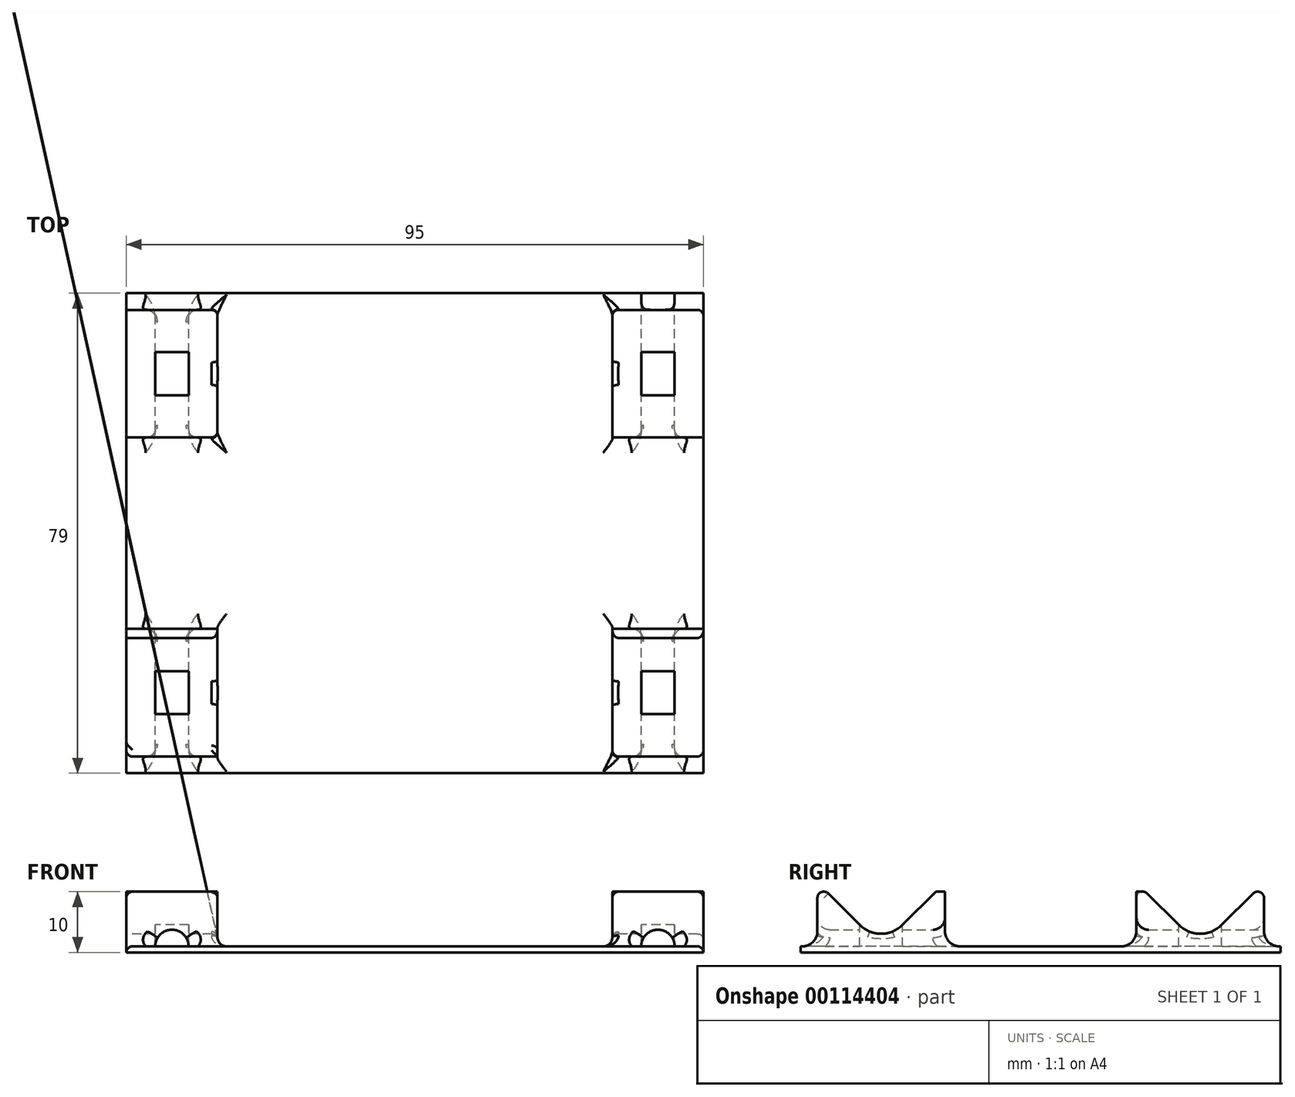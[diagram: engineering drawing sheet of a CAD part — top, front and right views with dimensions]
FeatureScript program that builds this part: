
annotation { "Feature Type Name" : "Feature", "Feature Type Description" : "" }
export const myFeature = defineFeature(function(context is Context, id is Id, definition is map)
    precondition{}
    {
        {
            var Q0;
            Q0=qCreatedBy(makeId("Top.planeOp"),FACE);
            var sketch = newSketch(context, id + "F0", { "sketchPlane" : qUnion([Q0])});
            skLineSegment(sketch, "E0.bottom", {"start": v(0, 0) * mm, "end": v(95, 0) * mm});
            skLineSegment(sketch, "E0.top", {"start": v(0, 79) * mm, "end": v(95, 79) * mm});
            skLineSegment(sketch, "E0.left", {"start": v(0, 0) * mm, "end": v(0, 79) * mm});
            skLineSegment(sketch, "E0.right", {"start": v(95, 0) * mm, "end": v(95, 79) * mm});
            skSolve(sketch);
        }
        {
            var Q0;
            Q0=makeQuery(id+"F0.imprint","IMPRINT",FACE,{"disambiguationData":[TD([[makeQuery(id+"F0.imprint","IMPRINT",EDGE,{"derivedFrom":sQuery(id+"F0.wireOp",EDGE,"E0.bottom")}),1.0]])]});
            extrude(context, id + "F1", {"entities" : qUnion([Q0]), "depth" : 10 * mm});
        }
        {
            var Q0;
            Q0=qCreatedBy(makeId("Right.planeOp"),FACE);
            var sketch = newSketch(context, id + "F2", { "sketchPlane" : qUnion([Q0])});
            skCircle(sketch, "E1", {"center": v(65.75, 10.55) * mm, "radius": 6.75 * mm, "construction": true});
            skLineSegment(sketch, "E2", {"start": v(79, 1) * mm, "end": v(0, 1) * mm, "construction": true});
            skLineSegment(sketch, "E3.0", {"start": v(79, 10) * mm, "end": v(79, 0) * mm, "construction": true});
            skLineSegment(sketch, "E4.0", {"start": v(0, 10) * mm, "end": v(0, 0) * mm, "construction": true});
            skLineSegment(sketch, "E5", {"start": v(79, 0) * mm, "end": v(0, 0) * mm, "construction": true});
            skLineSegment(sketch, "E6", {"start": v(39.5, 0) * mm, "end": v(39.5, 0) * mm});
            skPoint(sketch, "E6.endSnap0", {"position": v(39.5, 0) * mm});
            skLineSegment(sketch, "E7.0", {"start": v(0, 10) * mm, "end": v(79, 10) * mm});
            skLineSegment(sketch, "E8", {"start": v(65.75, 1) * mm, "end": v(74.75, 10) * mm});
            skLineSegment(sketch, "E9", {"start": v(65.75, 1) * mm, "end": v(56.75, 10) * mm});
            skLineSegment(sketch, "E10", {"start": v(39.5, 0) * mm, "end": v(39.5, 10) * mm, "construction": true});
            skLineSegment(sketch, "E11", {"start": v(74.75, 10) * mm, "end": v(76.25, 10) * mm, "construction": true});
            skLineSegment(sketch, "E12", {"start": v(76.25, 10) * mm, "end": v(76.25, 1) * mm});
            skLineSegment(sketch, "E13", {"start": v(76.25, 1) * mm, "end": v(79, 1) * mm});
            skLineSegment(sketch, "E14", {"start": v(79, 10) * mm, "end": v(76.25, 10) * mm});
            skLineSegment(sketch, "E15", {"start": v(79, 10) * mm, "end": v(79, 1) * mm});
            skLineSegment(sketch, "E16", {"start": v(56.75, 10) * mm, "end": v(55.25, 10) * mm, "construction": true});
            skLineSegment(sketch, "E17", {"start": v(55.25, 10) * mm, "end": v(55.25, 1) * mm});
            skLineSegment(sketch, "E18", {"start": v(55.25, 1) * mm, "end": v(39.5, 1) * mm});
            skLineSegment(sketch, "E19.MirrorCS", {"start": v(0, 10) * mm, "end": v(2.75, 10) * mm});
            skLineSegment(sketch, "E20.MirrorCS", {"start": v(2.75, 10) * mm, "end": v(2.75, 1) * mm});
            skLineSegment(sketch, "E21.MirrorCS", {"start": v(13.25, 1) * mm, "end": v(4.25, 10) * mm});
            skLineSegment(sketch, "E22.MirrorCS", {"start": v(13.25, 1) * mm, "end": v(22.25, 10) * mm});
            skLineSegment(sketch, "E23.MirrorCS", {"start": v(4.25, 10) * mm, "end": v(2.75, 10) * mm});
            skLineSegment(sketch, "E24.MirrorCS", {"start": v(22.25, 10) * mm, "end": v(23.75, 10) * mm});
            skLineSegment(sketch, "E25.MirrorCS", {"start": v(23.75, 10) * mm, "end": v(23.75, 1) * mm});
            skLineSegment(sketch, "E26.MirrorCS", {"start": v(2.75, 1) * mm, "end": v(0, 1) * mm});
            skLineSegment(sketch, "E27.MirrorCS", {"start": v(0, 10) * mm, "end": v(0, 1) * mm});
            skLineSegment(sketch, "E28.MirrorCS", {"start": v(23.75, 1) * mm, "end": v(39.5, 1) * mm});
            skLineSegment(sketch, "E29", {"start": v(39.5, 10) * mm, "end": v(39.5, 15.62) * mm, "construction": true});
            skSolve(sketch);
        }
        {
            var Q0;
            Q0 = qSketchRegion(id + "F2", true);
            extrude(context, id + "F3", {"entities" : qUnion([Q0]), "operationType" : NewBodyOperationType.REMOVE, "endBound" : BoundingType.THROUGH_ALL, "depth" : 25 * mm});
        }
        {
            var Q0;
            Q0=makeQuery(id+"F3.boolean.opBoolean","COPY",EDGE,{"derivedFrom":makeQuery(id+"F3.opExtrude","SWEPT_EDGE",EDGE,{"disambiguationData":[OSD([sQuery(id+"F2.wireOp",EDGE,"E8"),sQuery(id+"F2.wireOp",EDGE,"E9")])]})});
            var Q1;
            Q1=makeQuery(id+"F3.boolean.opBoolean","COPY",EDGE,{"derivedFrom":makeQuery(id+"F3.opExtrude","SWEPT_EDGE",EDGE,{"disambiguationData":[OSD([sQuery(id+"F2.wireOp",EDGE,"E21.MirrorCS"),sQuery(id+"F2.wireOp",EDGE,"E22.MirrorCS")])]})});
            fillet(context, id + "F4", {"entities" : qUnion([Q0, Q1]), "radius" : 5 * mm, "tangentPropagation" : true, "allowEdgeOverflow" : false});
        }
        {
            var Q0;
            Q0=qCreatedBy(makeId("Front.planeOp"),FACE);
            var sketch = newSketch(context, id + "F5", { "sketchPlane" : qUnion([Q0])});
            skLineSegment(sketch, "E30.top", {"start": v(15, 10) * mm, "end": v(80, 10) * mm});
            skLineSegment(sketch, "E30.left", {"start": v(15, 1) * mm, "end": v(15, 10) * mm});
            skLineSegment(sketch, "E30.right", {"start": v(80, 1) * mm, "end": v(80, 10) * mm});
            skLineSegment(sketch, "E31.0", {"start": v(95, 1) * mm, "end": v(0, 1) * mm});
            skSolve(sketch);
        }
        {
            var Q0;
            Q0=makeQuery(id+"F5.imprint","IMPRINT",FACE,{"disambiguationData":[TD([[makeQuery(id+"F5.imprint","IMPRINT",EDGE,{"derivedFrom":sQuery(id+"F5.wireOp",EDGE,"E30.top")}),-1.0]])]});
            extrude(context, id + "F6", {"entities" : qUnion([Q0]), "operationType" : NewBodyOperationType.REMOVE, "endBound" : BoundingType.THROUGH_ALL, "oppositeDirection" : true, "depth" : 25 * mm});
        }
        {
            var Q0;
            {var subQ0=sQuery(id+"F0.wireOp",EDGE,"E0.left");Q0=makeQuery(id+"F6.boolean.opBoolean","SPLIT",FACE,{"disambiguationData":[TD([makeQuery(id+"F1.opExtrude","SWEPT_FACE",FACE,{"disambiguationData":[OSD([subQ0])]})])],"derivedFrom":makeQuery(id+"F3.boolean.opBoolean","COPY",FACE,{"derivedFrom":makeQuery(id+"F3.opExtrude","SWEPT_FACE",FACE,{"disambiguationData":[OSD([sQuery(id+"F2.wireOp",EDGE,"E12")])]})})});}
            var sketch = newSketch(context, id + "F7", { "sketchPlane" : qUnion([Q0])});
            skLineSegment(sketch, "E32.0", {"start": v(-15, 10) * mm, "end": v(-15, 1) * mm, "construction": true});
            skLineSegment(sketch, "E33.0", {"start": v(0, 10) * mm, "end": v(0, 1) * mm, "construction": true});
            skLineSegment(sketch, "E34.0", {"start": v(-15, 10) * mm, "end": v(0, 10) * mm, "construction": true});
            skLineSegment(sketch, "E35.0", {"start": v(-15, 1) * mm, "end": v(0, 1) * mm, "construction": true});
            skLineSegment(sketch, "E36.0", {"start": v(-95, 10) * mm, "end": v(-95, 1) * mm, "construction": true});
            skLineSegment(sketch, "E37.0", {"start": v(-80, 10) * mm, "end": v(-80, 1) * mm, "construction": true});
            skLineSegment(sketch, "E38.0", {"start": v(-95, 1) * mm, "end": v(-80, 1) * mm, "construction": true});
            skLineSegment(sketch, "E39.0", {"start": v(-95, 10) * mm, "end": v(-80, 10) * mm, "construction": true});
            skArc(sketch, "E40", {"start": v(-84.75, 1) * mm, "mid": v(-87.5, 3.75) * mm, "end": v(-90.25, 1) * mm});
            skLineSegment(sketch, "E41", {"start": v(-90.25, 1) * mm, "end": v(-84.75, 1) * mm});
            skArc(sketch, "E42", {"start": v(-4.75, 1) * mm, "mid": v(-7.5, 3.75) * mm, "end": v(-10.25, 1) * mm});
            skLineSegment(sketch, "E43", {"start": v(-10.25, 1) * mm, "end": v(-4.75, 1) * mm});
            skSolve(sketch);
        }
        {
            var Q0;
            Q0 = qSketchRegion(id + "F7", true);
            extrude(context, id + "F8", {"entities" : qUnion([Q0]), "operationType" : NewBodyOperationType.REMOVE, "endBound" : BoundingType.THROUGH_ALL, "oppositeDirection" : true, "depth" : 25 * mm});
        }
        {
            var Q0;
            {var subQ0=sQuery(id+"F0.wireOp",EDGE,"E0.right");var subQ1=makeQuery(id+"F1.opExtrude","SWEPT_FACE",FACE,{"disambiguationData":[OSD([subQ0])]});var subQ2=makeQuery(id+"F3.opExtrude","SWEPT_FACE",FACE,{"disambiguationData":[OSD([sQuery(id+"F2.wireOp",EDGE,"E20.MirrorCS")])]});var subQ4=sQuery(id+"F0.wireOp",EDGE,"E0.left");Q0=makeQuery(id+"F6.boolean.opBoolean","SPLIT",FACE,{"disambiguationData":[TD([subQ1])],"derivedFrom":makeQuery(id+"F3.boolean.opBoolean","SPLIT",FACE,{"disambiguationData":[TD([subQ2])],"derivedFrom":makeQuery(id+"F1.opExtrude","CAP_FACE",FACE,{"disambiguationData":[OSD([sQuery(id+"F0.wireOp",EDGE,"E0.bottom"),sQuery(id+"F0.wireOp",EDGE,"E0.top"),subQ4,subQ0])],"isStart":false})})});}
            var sketch = newSketch(context, id + "F9", { "sketchPlane" : qUnion([Q0])});
            skLineSegment(sketch, "E44.0", {"start": v(95, 62.21) * mm, "end": v(80, 62.21) * mm});
            skLineSegment(sketch, "E45.0", {"start": v(80, 69.29) * mm, "end": v(95, 69.29) * mm});
            skLineSegment(sketch, "E46", {"start": v(87.5, 62.21) * mm, "end": v(87.5, 69.29) * mm, "construction": true});
            skLineSegment(sketch, "E47.bottom", {"start": v(90.25, 62.21) * mm, "end": v(84.75, 62.21) * mm});
            skLineSegment(sketch, "E47.top", {"start": v(90.25, 69.29) * mm, "end": v(84.75, 69.29) * mm});
            skLineSegment(sketch, "E47.left", {"start": v(90.25, 62.21) * mm, "end": v(90.25, 69.29) * mm});
            skLineSegment(sketch, "E47.right", {"start": v(84.75, 62.21) * mm, "end": v(84.75, 69.29) * mm});
            skLineSegment(sketch, "E48.0", {"start": v(95, 9.71) * mm, "end": v(80, 9.71) * mm, "construction": true});
            skLineSegment(sketch, "E48.1", {"start": v(80, 16.79) * mm, "end": v(95, 16.79) * mm, "construction": true});
            skLineSegment(sketch, "E49", {"start": v(87.5, 9.71) * mm, "end": v(87.5, 16.79) * mm, "construction": true});
            skLineSegment(sketch, "E50.bottom", {"start": v(90.25, 9.71) * mm, "end": v(84.75, 9.71) * mm});
            skLineSegment(sketch, "E50.top", {"start": v(90.25, 16.79) * mm, "end": v(84.75, 16.79) * mm});
            skLineSegment(sketch, "E50.left", {"start": v(90.25, 9.71) * mm, "end": v(90.25, 16.79) * mm});
            skLineSegment(sketch, "E50.right", {"start": v(84.75, 9.71) * mm, "end": v(84.75, 16.79) * mm});
            skLineSegment(sketch, "E51.0", {"start": v(15, 9.71) * mm, "end": v(0, 9.71) * mm});
            skLineSegment(sketch, "E51.1", {"start": v(0, 16.79) * mm, "end": v(15, 16.79) * mm});
            skLineSegment(sketch, "E51.2", {"start": v(15, 62.21) * mm, "end": v(0, 62.21) * mm});
            skLineSegment(sketch, "E51.3", {"start": v(0, 69.29) * mm, "end": v(15, 69.29) * mm});
            skLineSegment(sketch, "E52", {"start": v(7.5, 9.71) * mm, "end": v(7.5, 69.29) * mm, "construction": true});
            skLineSegment(sketch, "E53.bottom", {"start": v(4.75, 69.29) * mm, "end": v(10.25, 69.29) * mm});
            skLineSegment(sketch, "E53.top", {"start": v(4.75, 62.21) * mm, "end": v(10.25, 62.21) * mm});
            skLineSegment(sketch, "E53.left", {"start": v(4.75, 69.29) * mm, "end": v(4.75, 62.21) * mm});
            skLineSegment(sketch, "E53.right", {"start": v(10.25, 69.29) * mm, "end": v(10.25, 62.21) * mm});
            skLineSegment(sketch, "E54.bottom", {"start": v(4.75, 16.79) * mm, "end": v(10.25, 16.79) * mm});
            skLineSegment(sketch, "E54.top", {"start": v(4.75, 9.71) * mm, "end": v(10.25, 9.71) * mm});
            skLineSegment(sketch, "E54.left", {"start": v(4.75, 16.79) * mm, "end": v(4.75, 9.71) * mm});
            skLineSegment(sketch, "E54.right", {"start": v(10.25, 16.79) * mm, "end": v(10.25, 9.71) * mm});
            skSolve(sketch);
        }
        {
            var Q0;
            Q0 = qSketchRegion(id + "F9", true);
            var Q1;
            Q1=makeQuery(id+"F8.boolean.opBoolean","MERGE",FACE,{"derivedFrom":[makeQuery(id+"F6.boolean.opBoolean","MERGE",FACE,{"derivedFrom":[makeQuery(id+"F3.boolean.opBoolean","COPY",FACE,{"derivedFrom":makeQuery(id+"F3.opExtrude","SWEPT_FACE",FACE,{"disambiguationData":[OSD([sQuery(id+"F2.wireOp",EDGE,"E13")])]})}),makeQuery(id+"F3.boolean.opBoolean","COPY",FACE,{"derivedFrom":makeQuery(id+"F3.opExtrude","SWEPT_FACE",FACE,{"disambiguationData":[OSD([sQuery(id+"F2.wireOp",EDGE,"E18"),sQuery(id+"F2.wireOp",EDGE,"E28.MirrorCS")])]})}),makeQuery(id+"F3.boolean.opBoolean","COPY",FACE,{"derivedFrom":makeQuery(id+"F3.opExtrude","SWEPT_FACE",FACE,{"disambiguationData":[OSD([sQuery(id+"F2.wireOp",EDGE,"E26.MirrorCS")])]})}),makeQuery(id+"F6.opExtrude","SWEPT_FACE",FACE,{"disambiguationData":[OSD([sQuery(id+"F5.wireOp",EDGE,"E31.0")])]})]}),makeQuery(id+"F8.opExtrude","SWEPT_FACE",FACE,{"disambiguationData":[OSD([sQuery(id+"F7.wireOp",EDGE,"E41")])]}),makeQuery(id+"F8.opExtrude","SWEPT_FACE",FACE,{"disambiguationData":[OSD([sQuery(id+"F7.wireOp",EDGE,"E43")])]})]});
            extrude(context, id + "F10", {"entities" : qUnion([Q0]), "operationType" : NewBodyOperationType.REMOVE, "endBound" : BoundingType.UP_TO_SURFACE, "oppositeDirection" : true, "endBoundEntityFace" : qUnion([Q1]), "depth" : 25 * mm});
        }
        {
            var Q0;
            {var subQ0=sQuery(id+"F2.wireOp",EDGE,"E25.MirrorCS");var subQ2=makeQuery(id+"F1.opExtrude","SWEPT_FACE",FACE,{"disambiguationData":[OSD([sQuery(id+"F0.wireOp",EDGE,"E0.right")])]});var subQ3=sQuery(id+"F2.wireOp",EDGE,"E28.MirrorCS");Q0=makeQuery(id+"F8.boolean.opBoolean","SPLIT",EDGE,{"disambiguationData":[TD([subQ2])],"derivedFrom":makeQuery(id+"F6.boolean.opBoolean","SPLIT",EDGE,{"disambiguationData":[TD([subQ2])],"derivedFrom":makeQuery(id+"F3.boolean.opBoolean","COPY",EDGE,{"derivedFrom":makeQuery(id+"F3.opExtrude","SWEPT_EDGE",EDGE,{"disambiguationData":[OSD([subQ0,subQ3])]})})})});}
            var Q1;
            {var subQ1=sQuery(id+"F2.wireOp",EDGE,"E25.MirrorCS");var subQ3=sQuery(id+"F2.wireOp",EDGE,"E28.MirrorCS");var subQ9=sQuery(id+"F0.wireOp",EDGE,"E0.right");var subQ10=makeQuery(id+"F6.opExtrude","SWEPT_FACE",FACE,{"disambiguationData":[OSD([sQuery(id+"F5.wireOp",EDGE,"E30.right")])]});Q1=makeQuery(id+"F8.boolean.opBoolean","SPLIT",EDGE,{"disambiguationData":[TD([makeQuery(id+"F6.boolean.opBoolean","COPY",FACE,{"disambiguationData":[TD([makeQuery(id+"F3.boolean.opBoolean","COPY",FACE,{"derivedFrom":makeQuery(id+"F3.opExtrude","SWEPT_FACE",FACE,{"disambiguationData":[OSD([sQuery(id+"F2.wireOp",EDGE,"E20.MirrorCS")])]})})])],"derivedFrom":subQ10})])],"derivedFrom":makeQuery(id+"F6.boolean.opBoolean","SPLIT",EDGE,{"disambiguationData":[TD([makeQuery(id+"F1.opExtrude","SWEPT_FACE",FACE,{"disambiguationData":[OSD([subQ9])]})])],"derivedFrom":makeQuery(id+"F3.boolean.opBoolean","COPY",EDGE,{"derivedFrom":makeQuery(id+"F3.opExtrude","SWEPT_EDGE",EDGE,{"disambiguationData":[OSD([subQ1,subQ3])]})})})});}
            var Q2;
            {var subQ1=sQuery(id+"F2.wireOp",EDGE,"E13");var subQ3=sQuery(id+"F2.wireOp",EDGE,"E12");var subQ5=makeQuery(id+"F1.opExtrude","SWEPT_FACE",FACE,{"disambiguationData":[OSD([sQuery(id+"F0.wireOp",EDGE,"E0.right")])]});Q2=makeQuery(id+"F8.boolean.opBoolean","SPLIT",EDGE,{"disambiguationData":[TD([subQ5])],"derivedFrom":makeQuery(id+"F6.boolean.opBoolean","SPLIT",EDGE,{"disambiguationData":[TD([subQ5])],"derivedFrom":makeQuery(id+"F3.boolean.opBoolean","COPY",EDGE,{"derivedFrom":makeQuery(id+"F3.opExtrude","SWEPT_EDGE",EDGE,{"disambiguationData":[OSD([subQ3,subQ1])]})})})});}
            var Q3;
            {var subQ2=sQuery(id+"F2.wireOp",EDGE,"E13");var subQ4=sQuery(id+"F2.wireOp",EDGE,"E12");var subQ8=sQuery(id+"F0.wireOp",EDGE,"E0.right");var subQ9=sQuery(id+"F2.wireOp",EDGE,"E8");var subQ10=makeQuery(id+"F6.opExtrude","SWEPT_FACE",FACE,{"disambiguationData":[OSD([sQuery(id+"F5.wireOp",EDGE,"E30.right")])]});Q3=makeQuery(id+"F8.boolean.opBoolean","SPLIT",EDGE,{"disambiguationData":[TD([makeQuery(id+"F6.boolean.opBoolean","COPY",FACE,{"disambiguationData":[TD([makeQuery(id+"F3.boolean.opBoolean","COPY",FACE,{"derivedFrom":makeQuery(id+"F3.opExtrude","SWEPT_FACE",FACE,{"disambiguationData":[OSD([subQ9])]})})])],"derivedFrom":subQ10})])],"derivedFrom":makeQuery(id+"F6.boolean.opBoolean","SPLIT",EDGE,{"disambiguationData":[TD([makeQuery(id+"F1.opExtrude","SWEPT_FACE",FACE,{"disambiguationData":[OSD([subQ8])]})])],"derivedFrom":makeQuery(id+"F3.boolean.opBoolean","COPY",EDGE,{"derivedFrom":makeQuery(id+"F3.opExtrude","SWEPT_EDGE",EDGE,{"disambiguationData":[OSD([subQ4,subQ2])]})})})});}
            var Q4;
            {var subQ2=sQuery(id+"F2.wireOp",EDGE,"E12");var subQ5=sQuery(id+"F0.wireOp",EDGE,"E0.left");var subQ6=sQuery(id+"F2.wireOp",EDGE,"E8");var subQ7=sQuery(id+"F2.wireOp",EDGE,"E13");var subQ10=makeQuery(id+"F6.opExtrude","SWEPT_FACE",FACE,{"disambiguationData":[OSD([sQuery(id+"F5.wireOp",EDGE,"E30.left")])]});Q4=makeQuery(id+"F8.boolean.opBoolean","SPLIT",EDGE,{"disambiguationData":[TD([makeQuery(id+"F6.boolean.opBoolean","COPY",FACE,{"disambiguationData":[TD([makeQuery(id+"F3.boolean.opBoolean","COPY",FACE,{"derivedFrom":makeQuery(id+"F3.opExtrude","SWEPT_FACE",FACE,{"disambiguationData":[OSD([subQ6])]})})])],"derivedFrom":subQ10})])],"derivedFrom":makeQuery(id+"F6.boolean.opBoolean","SPLIT",EDGE,{"disambiguationData":[TD([makeQuery(id+"F1.opExtrude","SWEPT_FACE",FACE,{"disambiguationData":[OSD([subQ5])]})])],"derivedFrom":makeQuery(id+"F3.boolean.opBoolean","COPY",EDGE,{"derivedFrom":makeQuery(id+"F3.opExtrude","SWEPT_EDGE",EDGE,{"disambiguationData":[OSD([subQ2,subQ7])]})})})});}
            var Q5;
            {var subQ1=sQuery(id+"F2.wireOp",EDGE,"E13");var subQ3=sQuery(id+"F2.wireOp",EDGE,"E12");var subQ5=makeQuery(id+"F1.opExtrude","SWEPT_FACE",FACE,{"disambiguationData":[OSD([sQuery(id+"F0.wireOp",EDGE,"E0.left")])]});Q5=makeQuery(id+"F8.boolean.opBoolean","SPLIT",EDGE,{"disambiguationData":[TD([subQ5])],"derivedFrom":makeQuery(id+"F6.boolean.opBoolean","SPLIT",EDGE,{"disambiguationData":[TD([subQ5])],"derivedFrom":makeQuery(id+"F3.boolean.opBoolean","COPY",EDGE,{"derivedFrom":makeQuery(id+"F3.opExtrude","SWEPT_EDGE",EDGE,{"disambiguationData":[OSD([subQ3,subQ1])]})})})});}
            var Q6;
            {var subQ1=sQuery(id+"F2.wireOp",EDGE,"E25.MirrorCS");var subQ3=sQuery(id+"F2.wireOp",EDGE,"E28.MirrorCS");var subQ8=sQuery(id+"F0.wireOp",EDGE,"E0.left");var subQ10=makeQuery(id+"F6.opExtrude","SWEPT_FACE",FACE,{"disambiguationData":[OSD([sQuery(id+"F5.wireOp",EDGE,"E30.left")])]});Q6=makeQuery(id+"F8.boolean.opBoolean","SPLIT",EDGE,{"disambiguationData":[TD([makeQuery(id+"F6.boolean.opBoolean","COPY",FACE,{"disambiguationData":[TD([makeQuery(id+"F3.boolean.opBoolean","COPY",FACE,{"derivedFrom":makeQuery(id+"F3.opExtrude","SWEPT_FACE",FACE,{"disambiguationData":[OSD([sQuery(id+"F2.wireOp",EDGE,"E20.MirrorCS")])]})})])],"derivedFrom":subQ10})])],"derivedFrom":makeQuery(id+"F6.boolean.opBoolean","SPLIT",EDGE,{"disambiguationData":[TD([makeQuery(id+"F1.opExtrude","SWEPT_FACE",FACE,{"disambiguationData":[OSD([subQ8])]})])],"derivedFrom":makeQuery(id+"F3.boolean.opBoolean","COPY",EDGE,{"derivedFrom":makeQuery(id+"F3.opExtrude","SWEPT_EDGE",EDGE,{"disambiguationData":[OSD([subQ1,subQ3])]})})})});}
            var Q7;
            {var subQ0=sQuery(id+"F2.wireOp",EDGE,"E25.MirrorCS");var subQ2=sQuery(id+"F2.wireOp",EDGE,"E28.MirrorCS");var subQ5=makeQuery(id+"F1.opExtrude","SWEPT_FACE",FACE,{"disambiguationData":[OSD([sQuery(id+"F0.wireOp",EDGE,"E0.left")])]});Q7=makeQuery(id+"F8.boolean.opBoolean","SPLIT",EDGE,{"disambiguationData":[TD([subQ5])],"derivedFrom":makeQuery(id+"F6.boolean.opBoolean","SPLIT",EDGE,{"disambiguationData":[TD([subQ5])],"derivedFrom":makeQuery(id+"F3.boolean.opBoolean","COPY",EDGE,{"derivedFrom":makeQuery(id+"F3.opExtrude","SWEPT_EDGE",EDGE,{"disambiguationData":[OSD([subQ0,subQ2])]})})})});}
            var Q8;
            {var subQ0=sQuery(id+"F2.wireOp",EDGE,"E20.MirrorCS");var subQ4=makeQuery(id+"F1.opExtrude","SWEPT_FACE",FACE,{"disambiguationData":[OSD([sQuery(id+"F0.wireOp",EDGE,"E0.right")])]});var subQ5=sQuery(id+"F2.wireOp",EDGE,"E26.MirrorCS");Q8=makeQuery(id+"F8.boolean.opBoolean","SPLIT",EDGE,{"disambiguationData":[TD([subQ4])],"derivedFrom":makeQuery(id+"F6.boolean.opBoolean","SPLIT",EDGE,{"disambiguationData":[TD([subQ4])],"derivedFrom":makeQuery(id+"F3.boolean.opBoolean","COPY",EDGE,{"derivedFrom":makeQuery(id+"F3.opExtrude","SWEPT_EDGE",EDGE,{"disambiguationData":[OSD([subQ0,subQ5])]})})})});}
            var Q9;
            {var subQ0=sQuery(id+"F2.wireOp",EDGE,"E26.MirrorCS");var subQ2=sQuery(id+"F2.wireOp",EDGE,"E20.MirrorCS");var subQ3=makeQuery(id+"F3.boolean.opBoolean","COPY",FACE,{"derivedFrom":makeQuery(id+"F3.opExtrude","SWEPT_FACE",FACE,{"disambiguationData":[OSD([subQ2])]})});var subQ9=sQuery(id+"F0.wireOp",EDGE,"E0.right");var subQ10=makeQuery(id+"F6.opExtrude","SWEPT_FACE",FACE,{"disambiguationData":[OSD([sQuery(id+"F5.wireOp",EDGE,"E30.right")])]});Q9=makeQuery(id+"F8.boolean.opBoolean","SPLIT",EDGE,{"disambiguationData":[TD([makeQuery(id+"F6.boolean.opBoolean","COPY",FACE,{"disambiguationData":[TD([subQ3])],"derivedFrom":subQ10})])],"derivedFrom":makeQuery(id+"F6.boolean.opBoolean","SPLIT",EDGE,{"disambiguationData":[TD([makeQuery(id+"F1.opExtrude","SWEPT_FACE",FACE,{"disambiguationData":[OSD([subQ9])]})])],"derivedFrom":makeQuery(id+"F3.boolean.opBoolean","COPY",EDGE,{"derivedFrom":makeQuery(id+"F3.opExtrude","SWEPT_EDGE",EDGE,{"disambiguationData":[OSD([subQ2,subQ0])]})})})});}
            var Q10;
            {var subQ0=sQuery(id+"F2.wireOp",EDGE,"E26.MirrorCS");var subQ2=sQuery(id+"F2.wireOp",EDGE,"E20.MirrorCS");var subQ3=makeQuery(id+"F3.boolean.opBoolean","COPY",FACE,{"derivedFrom":makeQuery(id+"F3.opExtrude","SWEPT_FACE",FACE,{"disambiguationData":[OSD([subQ2])]})});var subQ8=sQuery(id+"F0.wireOp",EDGE,"E0.left");var subQ10=makeQuery(id+"F6.opExtrude","SWEPT_FACE",FACE,{"disambiguationData":[OSD([sQuery(id+"F5.wireOp",EDGE,"E30.left")])]});Q10=makeQuery(id+"F8.boolean.opBoolean","SPLIT",EDGE,{"disambiguationData":[TD([makeQuery(id+"F6.boolean.opBoolean","COPY",FACE,{"disambiguationData":[TD([subQ3])],"derivedFrom":subQ10})])],"derivedFrom":makeQuery(id+"F6.boolean.opBoolean","SPLIT",EDGE,{"disambiguationData":[TD([makeQuery(id+"F1.opExtrude","SWEPT_FACE",FACE,{"disambiguationData":[OSD([subQ8])]})])],"derivedFrom":makeQuery(id+"F3.boolean.opBoolean","COPY",EDGE,{"derivedFrom":makeQuery(id+"F3.opExtrude","SWEPT_EDGE",EDGE,{"disambiguationData":[OSD([subQ2,subQ0])]})})})});}
            var Q11;
            {var subQ0=sQuery(id+"F2.wireOp",EDGE,"E20.MirrorCS");var subQ4=makeQuery(id+"F1.opExtrude","SWEPT_FACE",FACE,{"disambiguationData":[OSD([sQuery(id+"F0.wireOp",EDGE,"E0.left")])]});var subQ5=sQuery(id+"F2.wireOp",EDGE,"E26.MirrorCS");Q11=makeQuery(id+"F8.boolean.opBoolean","SPLIT",EDGE,{"disambiguationData":[TD([subQ4])],"derivedFrom":makeQuery(id+"F6.boolean.opBoolean","SPLIT",EDGE,{"disambiguationData":[TD([subQ4])],"derivedFrom":makeQuery(id+"F3.boolean.opBoolean","COPY",EDGE,{"derivedFrom":makeQuery(id+"F3.opExtrude","SWEPT_EDGE",EDGE,{"disambiguationData":[OSD([subQ0,subQ5])]})})})});}
            var Q12;
            {var subQ0=sQuery(id+"F2.wireOp",EDGE,"E18");var subQ2=sQuery(id+"F2.wireOp",EDGE,"E17");var subQ5=makeQuery(id+"F1.opExtrude","SWEPT_FACE",FACE,{"disambiguationData":[OSD([sQuery(id+"F0.wireOp",EDGE,"E0.left")])]});Q12=makeQuery(id+"F8.boolean.opBoolean","SPLIT",EDGE,{"disambiguationData":[TD([subQ5])],"derivedFrom":makeQuery(id+"F6.boolean.opBoolean","SPLIT",EDGE,{"disambiguationData":[TD([subQ5])],"derivedFrom":makeQuery(id+"F3.boolean.opBoolean","COPY",EDGE,{"derivedFrom":makeQuery(id+"F3.opExtrude","SWEPT_EDGE",EDGE,{"disambiguationData":[OSD([subQ2,subQ0])]})})})});}
            var Q13;
            {var subQ1=sQuery(id+"F2.wireOp",EDGE,"E18");var subQ4=sQuery(id+"F0.wireOp",EDGE,"E0.left");var subQ5=sQuery(id+"F2.wireOp",EDGE,"E8");var subQ7=sQuery(id+"F2.wireOp",EDGE,"E17");var subQ10=makeQuery(id+"F6.opExtrude","SWEPT_FACE",FACE,{"disambiguationData":[OSD([sQuery(id+"F5.wireOp",EDGE,"E30.left")])]});Q13=makeQuery(id+"F8.boolean.opBoolean","SPLIT",EDGE,{"disambiguationData":[TD([makeQuery(id+"F6.boolean.opBoolean","COPY",FACE,{"disambiguationData":[TD([makeQuery(id+"F3.boolean.opBoolean","COPY",FACE,{"derivedFrom":makeQuery(id+"F3.opExtrude","SWEPT_FACE",FACE,{"disambiguationData":[OSD([subQ5])]})})])],"derivedFrom":subQ10})])],"derivedFrom":makeQuery(id+"F6.boolean.opBoolean","SPLIT",EDGE,{"disambiguationData":[TD([makeQuery(id+"F1.opExtrude","SWEPT_FACE",FACE,{"disambiguationData":[OSD([subQ4])]})])],"derivedFrom":makeQuery(id+"F3.boolean.opBoolean","COPY",EDGE,{"derivedFrom":makeQuery(id+"F3.opExtrude","SWEPT_EDGE",EDGE,{"disambiguationData":[OSD([subQ7,subQ1])]})})})});}
            var Q14;
            {var subQ1=sQuery(id+"F2.wireOp",EDGE,"E18");var subQ3=sQuery(id+"F2.wireOp",EDGE,"E17");var subQ8=sQuery(id+"F0.wireOp",EDGE,"E0.right");var subQ9=sQuery(id+"F2.wireOp",EDGE,"E8");var subQ10=makeQuery(id+"F6.opExtrude","SWEPT_FACE",FACE,{"disambiguationData":[OSD([sQuery(id+"F5.wireOp",EDGE,"E30.right")])]});Q14=makeQuery(id+"F8.boolean.opBoolean","SPLIT",EDGE,{"disambiguationData":[TD([makeQuery(id+"F6.boolean.opBoolean","COPY",FACE,{"disambiguationData":[TD([makeQuery(id+"F3.boolean.opBoolean","COPY",FACE,{"derivedFrom":makeQuery(id+"F3.opExtrude","SWEPT_FACE",FACE,{"disambiguationData":[OSD([subQ9])]})})])],"derivedFrom":subQ10})])],"derivedFrom":makeQuery(id+"F6.boolean.opBoolean","SPLIT",EDGE,{"disambiguationData":[TD([makeQuery(id+"F1.opExtrude","SWEPT_FACE",FACE,{"disambiguationData":[OSD([subQ8])]})])],"derivedFrom":makeQuery(id+"F3.boolean.opBoolean","COPY",EDGE,{"derivedFrom":makeQuery(id+"F3.opExtrude","SWEPT_EDGE",EDGE,{"disambiguationData":[OSD([subQ3,subQ1])]})})})});}
            var Q15;
            {var subQ0=sQuery(id+"F2.wireOp",EDGE,"E18");var subQ2=sQuery(id+"F2.wireOp",EDGE,"E17");var subQ5=makeQuery(id+"F1.opExtrude","SWEPT_FACE",FACE,{"disambiguationData":[OSD([sQuery(id+"F0.wireOp",EDGE,"E0.right")])]});Q15=makeQuery(id+"F8.boolean.opBoolean","SPLIT",EDGE,{"disambiguationData":[TD([subQ5])],"derivedFrom":makeQuery(id+"F6.boolean.opBoolean","SPLIT",EDGE,{"disambiguationData":[TD([subQ5])],"derivedFrom":makeQuery(id+"F3.boolean.opBoolean","COPY",EDGE,{"derivedFrom":makeQuery(id+"F3.opExtrude","SWEPT_EDGE",EDGE,{"disambiguationData":[OSD([subQ2,subQ0])]})})})});}
            fillet(context, id + "F11", {"entities" : qUnion([Q0, Q1, Q2, Q3, Q4, Q5, Q6, Q7, Q8, Q9, Q10, Q11, Q12, Q13, Q14, Q15]), "radius" : 2.5 * mm, "tangentPropagation" : true, "allowEdgeOverflow" : false});
        }
        {
            var Q0;
            {var subQ0=sQuery(id+"F0.wireOp",EDGE,"E0.left");var subQ1=sQuery(id+"F2.wireOp",EDGE,"E9");Q0=makeQuery(id+"F6.boolean.opBoolean","SPLIT",EDGE,{"disambiguationData":[TD([makeQuery(id+"F1.opExtrude","SWEPT_FACE",FACE,{"disambiguationData":[OSD([subQ0])]})])],"derivedFrom":makeQuery(id+"F3.boolean.opBoolean","COPY",EDGE,{"derivedFrom":makeQuery(id+"F3.opExtrude","SWEPT_EDGE",EDGE,{"disambiguationData":[OSD([sQuery(id+"F2.wireOp",EDGE,"E7.0"),subQ1])]})})});}
            var Q1;
            {var subQ0=sQuery(id+"F0.wireOp",EDGE,"E0.left");var subQ1=sQuery(id+"F2.wireOp",EDGE,"E17");Q1=makeQuery(id+"F6.boolean.opBoolean","SPLIT",EDGE,{"disambiguationData":[TD([makeQuery(id+"F1.opExtrude","SWEPT_FACE",FACE,{"disambiguationData":[OSD([subQ0])]})])],"derivedFrom":makeQuery(id+"F3.boolean.opBoolean","COPY",EDGE,{"derivedFrom":makeQuery(id+"F3.opExtrude","SWEPT_EDGE",EDGE,{"disambiguationData":[OSD([sQuery(id+"F2.wireOp",EDGE,"E7.0"),subQ1])]})})});}
            var Q2;
            {var subQ0=sQuery(id+"F0.wireOp",EDGE,"E0.left");var subQ1=sQuery(id+"F2.wireOp",EDGE,"E8");Q2=makeQuery(id+"F6.boolean.opBoolean","SPLIT",EDGE,{"disambiguationData":[TD([makeQuery(id+"F1.opExtrude","SWEPT_FACE",FACE,{"disambiguationData":[OSD([subQ0])]})])],"derivedFrom":makeQuery(id+"F3.boolean.opBoolean","COPY",EDGE,{"derivedFrom":makeQuery(id+"F3.opExtrude","SWEPT_EDGE",EDGE,{"disambiguationData":[OSD([sQuery(id+"F2.wireOp",EDGE,"E7.0"),subQ1])]})})});}
            var Q3;
            {var subQ0=sQuery(id+"F0.wireOp",EDGE,"E0.left");var subQ1=sQuery(id+"F2.wireOp",EDGE,"E12");Q3=makeQuery(id+"F6.boolean.opBoolean","SPLIT",EDGE,{"disambiguationData":[TD([makeQuery(id+"F1.opExtrude","SWEPT_FACE",FACE,{"disambiguationData":[OSD([subQ0])]})])],"derivedFrom":makeQuery(id+"F3.boolean.opBoolean","COPY",EDGE,{"derivedFrom":makeQuery(id+"F3.opExtrude","SWEPT_EDGE",EDGE,{"disambiguationData":[OSD([subQ1,sQuery(id+"F2.wireOp",EDGE,"E14")])]})})});}
            var Q4;
            {var subQ0=sQuery(id+"F0.wireOp",EDGE,"E0.right");var subQ1=sQuery(id+"F2.wireOp",EDGE,"E12");Q4=makeQuery(id+"F6.boolean.opBoolean","SPLIT",EDGE,{"disambiguationData":[TD([makeQuery(id+"F1.opExtrude","SWEPT_FACE",FACE,{"disambiguationData":[OSD([subQ0])]})])],"derivedFrom":makeQuery(id+"F3.boolean.opBoolean","COPY",EDGE,{"derivedFrom":makeQuery(id+"F3.opExtrude","SWEPT_EDGE",EDGE,{"disambiguationData":[OSD([subQ1,sQuery(id+"F2.wireOp",EDGE,"E14")])]})})});}
            var Q5;
            {var subQ0=sQuery(id+"F0.wireOp",EDGE,"E0.right");var subQ1=sQuery(id+"F2.wireOp",EDGE,"E8");Q5=makeQuery(id+"F6.boolean.opBoolean","SPLIT",EDGE,{"disambiguationData":[TD([makeQuery(id+"F1.opExtrude","SWEPT_FACE",FACE,{"disambiguationData":[OSD([subQ0])]})])],"derivedFrom":makeQuery(id+"F3.boolean.opBoolean","COPY",EDGE,{"derivedFrom":makeQuery(id+"F3.opExtrude","SWEPT_EDGE",EDGE,{"disambiguationData":[OSD([sQuery(id+"F2.wireOp",EDGE,"E7.0"),subQ1])]})})});}
            var Q6;
            {var subQ0=sQuery(id+"F0.wireOp",EDGE,"E0.right");var subQ1=sQuery(id+"F2.wireOp",EDGE,"E9");Q6=makeQuery(id+"F6.boolean.opBoolean","SPLIT",EDGE,{"disambiguationData":[TD([makeQuery(id+"F1.opExtrude","SWEPT_FACE",FACE,{"disambiguationData":[OSD([subQ0])]})])],"derivedFrom":makeQuery(id+"F3.boolean.opBoolean","COPY",EDGE,{"derivedFrom":makeQuery(id+"F3.opExtrude","SWEPT_EDGE",EDGE,{"disambiguationData":[OSD([sQuery(id+"F2.wireOp",EDGE,"E7.0"),subQ1])]})})});}
            var Q7;
            {var subQ0=sQuery(id+"F0.wireOp",EDGE,"E0.right");var subQ1=sQuery(id+"F2.wireOp",EDGE,"E25.MirrorCS");Q7=makeQuery(id+"F6.boolean.opBoolean","SPLIT",EDGE,{"disambiguationData":[TD([makeQuery(id+"F1.opExtrude","SWEPT_FACE",FACE,{"disambiguationData":[OSD([subQ0])]})])],"derivedFrom":makeQuery(id+"F3.boolean.opBoolean","COPY",EDGE,{"derivedFrom":makeQuery(id+"F3.opExtrude","SWEPT_EDGE",EDGE,{"disambiguationData":[OSD([sQuery(id+"F2.wireOp",EDGE,"E7.0"),subQ1])]})})});}
            var Q8;
            {var subQ0=sQuery(id+"F0.wireOp",EDGE,"E0.right");var subQ1=sQuery(id+"F2.wireOp",EDGE,"E22.MirrorCS");Q8=makeQuery(id+"F6.boolean.opBoolean","SPLIT",EDGE,{"disambiguationData":[TD([makeQuery(id+"F1.opExtrude","SWEPT_FACE",FACE,{"disambiguationData":[OSD([subQ0])]})])],"derivedFrom":makeQuery(id+"F3.boolean.opBoolean","COPY",EDGE,{"derivedFrom":makeQuery(id+"F3.opExtrude","SWEPT_EDGE",EDGE,{"disambiguationData":[OSD([sQuery(id+"F2.wireOp",EDGE,"E7.0"),subQ1])]})})});}
            var Q9;
            {var subQ0=sQuery(id+"F0.wireOp",EDGE,"E0.right");var subQ1=sQuery(id+"F2.wireOp",EDGE,"E21.MirrorCS");Q9=makeQuery(id+"F6.boolean.opBoolean","SPLIT",EDGE,{"disambiguationData":[TD([makeQuery(id+"F1.opExtrude","SWEPT_FACE",FACE,{"disambiguationData":[OSD([subQ0])]})])],"derivedFrom":makeQuery(id+"F3.boolean.opBoolean","COPY",EDGE,{"derivedFrom":makeQuery(id+"F3.opExtrude","SWEPT_EDGE",EDGE,{"disambiguationData":[OSD([sQuery(id+"F2.wireOp",EDGE,"E7.0"),subQ1])]})})});}
            var Q10;
            {var subQ0=sQuery(id+"F0.wireOp",EDGE,"E0.right");var subQ1=sQuery(id+"F2.wireOp",EDGE,"E20.MirrorCS");Q10=makeQuery(id+"F6.boolean.opBoolean","SPLIT",EDGE,{"disambiguationData":[TD([makeQuery(id+"F1.opExtrude","SWEPT_FACE",FACE,{"disambiguationData":[OSD([subQ0])]})])],"derivedFrom":makeQuery(id+"F3.boolean.opBoolean","COPY",EDGE,{"derivedFrom":makeQuery(id+"F3.opExtrude","SWEPT_EDGE",EDGE,{"disambiguationData":[OSD([sQuery(id+"F2.wireOp",EDGE,"E19.MirrorCS"),subQ1])]})})});}
            var Q11;
            {var subQ0=sQuery(id+"F0.wireOp",EDGE,"E0.left");var subQ1=sQuery(id+"F2.wireOp",EDGE,"E20.MirrorCS");Q11=makeQuery(id+"F6.boolean.opBoolean","SPLIT",EDGE,{"disambiguationData":[TD([makeQuery(id+"F1.opExtrude","SWEPT_FACE",FACE,{"disambiguationData":[OSD([subQ0])]})])],"derivedFrom":makeQuery(id+"F3.boolean.opBoolean","COPY",EDGE,{"derivedFrom":makeQuery(id+"F3.opExtrude","SWEPT_EDGE",EDGE,{"disambiguationData":[OSD([sQuery(id+"F2.wireOp",EDGE,"E19.MirrorCS"),subQ1])]})})});}
            var Q12;
            {var subQ0=sQuery(id+"F0.wireOp",EDGE,"E0.left");var subQ1=makeQuery(id+"F1.opExtrude","SWEPT_FACE",FACE,{"disambiguationData":[OSD([subQ0])]});var subQ2=makeQuery(id+"F3.opExtrude","SWEPT_FACE",FACE,{"disambiguationData":[OSD([sQuery(id+"F2.wireOp",EDGE,"E20.MirrorCS")])]});var subQ4=sQuery(id+"F0.wireOp",EDGE,"E0.right");Q12=makeQuery(id+"F6.boolean.opBoolean","SPLIT",FACE,{"disambiguationData":[TD([subQ1])],"derivedFrom":makeQuery(id+"F3.boolean.opBoolean","SPLIT",FACE,{"disambiguationData":[TD([subQ2])],"derivedFrom":makeQuery(id+"F1.opExtrude","CAP_FACE",FACE,{"disambiguationData":[OSD([sQuery(id+"F0.wireOp",EDGE,"E0.bottom"),sQuery(id+"F0.wireOp",EDGE,"E0.top"),subQ0,subQ4])],"isStart":false})})});}
            var Q13;
            {var subQ0=sQuery(id+"F0.wireOp",EDGE,"E0.left");var subQ1=sQuery(id+"F2.wireOp",EDGE,"E22.MirrorCS");Q13=makeQuery(id+"F6.boolean.opBoolean","SPLIT",EDGE,{"disambiguationData":[TD([makeQuery(id+"F1.opExtrude","SWEPT_FACE",FACE,{"disambiguationData":[OSD([subQ0])]})])],"derivedFrom":makeQuery(id+"F3.boolean.opBoolean","COPY",EDGE,{"derivedFrom":makeQuery(id+"F3.opExtrude","SWEPT_EDGE",EDGE,{"disambiguationData":[OSD([sQuery(id+"F2.wireOp",EDGE,"E7.0"),subQ1])]})})});}
            fillet(context, id + "F12", {"entities" : qUnion([Q0, Q1, Q2, Q3, Q4, Q5, Q6, Q7, Q8, Q9, Q10, Q11, Q12, Q13]), "radius" : 1 * mm, "tangentPropagation" : true, "allowEdgeOverflow" : false});
        }
        {
            var Q0;
            {var subQ0=sQuery(id+"F5.wireOp",EDGE,"E30.right");var subQ1=sQuery(id+"F5.wireOp",EDGE,"E31.0");Q0=makeQuery(id+"F6.boolean.opBoolean","COPY",EDGE,{"disambiguationData":[TD([makeQuery(id+"F3.boolean.opBoolean","COPY",FACE,{"derivedFrom":makeQuery(id+"F3.opExtrude","SWEPT_FACE",FACE,{"disambiguationData":[OSD([sQuery(id+"F2.wireOp",EDGE,"E20.MirrorCS")])]})})])],"derivedFrom":makeQuery(id+"F6.opExtrude","SWEPT_EDGE",EDGE,{"disambiguationData":[OSD([subQ0,subQ1])]})});}
            var Q1;
            {var subQ0=sQuery(id+"F5.wireOp",EDGE,"E30.right");var subQ1=sQuery(id+"F5.wireOp",EDGE,"E31.0");Q1=makeQuery(id+"F6.boolean.opBoolean","COPY",EDGE,{"disambiguationData":[TD([makeQuery(id+"F3.boolean.opBoolean","COPY",FACE,{"derivedFrom":makeQuery(id+"F3.opExtrude","SWEPT_FACE",FACE,{"disambiguationData":[OSD([sQuery(id+"F2.wireOp",EDGE,"E12")])]})})])],"derivedFrom":makeQuery(id+"F6.opExtrude","SWEPT_EDGE",EDGE,{"disambiguationData":[OSD([subQ0,subQ1])]})});}
            var Q2;
            {var subQ0=sQuery(id+"F5.wireOp",EDGE,"E30.left");var subQ1=sQuery(id+"F5.wireOp",EDGE,"E31.0");Q2=makeQuery(id+"F6.boolean.opBoolean","COPY",EDGE,{"disambiguationData":[TD([makeQuery(id+"F3.boolean.opBoolean","COPY",FACE,{"derivedFrom":makeQuery(id+"F3.opExtrude","SWEPT_FACE",FACE,{"disambiguationData":[OSD([sQuery(id+"F2.wireOp",EDGE,"E20.MirrorCS")])]})})])],"derivedFrom":makeQuery(id+"F6.opExtrude","SWEPT_EDGE",EDGE,{"disambiguationData":[OSD([subQ0,subQ1])]})});}
            var Q3;
            {var subQ0=sQuery(id+"F5.wireOp",EDGE,"E30.left");var subQ1=sQuery(id+"F5.wireOp",EDGE,"E31.0");Q3=makeQuery(id+"F6.boolean.opBoolean","COPY",EDGE,{"disambiguationData":[TD([makeQuery(id+"F3.boolean.opBoolean","COPY",FACE,{"derivedFrom":makeQuery(id+"F3.opExtrude","SWEPT_FACE",FACE,{"disambiguationData":[OSD([sQuery(id+"F2.wireOp",EDGE,"E12")])]})})])],"derivedFrom":makeQuery(id+"F6.opExtrude","SWEPT_EDGE",EDGE,{"disambiguationData":[OSD([subQ0,subQ1])]})});}
            fillet(context, id + "F13", {"entities" : qUnion([Q0, Q1, Q2, Q3]), "radius" : 1.5 * mm, "allowEdgeOverflow" : false});
        }
        {
            var Q0;
            Q0=makeQuery(id+"F6.boolean.opBoolean","INTERSECT",EDGE,{"derivedFrom":[makeQuery(id+"F3.boolean.opBoolean","COPY",FACE,{"derivedFrom":makeQuery(id+"F3.opExtrude","SWEPT_FACE",FACE,{"disambiguationData":[OSD([sQuery(id+"F2.wireOp",EDGE,"E22.MirrorCS")])]})}),makeQuery(id+"F6.opExtrude","SWEPT_FACE",FACE,{"disambiguationData":[OSD([sQuery(id+"F5.wireOp",EDGE,"E30.right")])]})]});
            var Q1;
            Q1=makeQuery(id+"F3.boolean.opBoolean","INTERSECT",EDGE,{"derivedFrom":[makeQuery(id+"F1.opExtrude","SWEPT_FACE",FACE,{"disambiguationData":[OSD([sQuery(id+"F0.wireOp",EDGE,"E0.right")])]}),makeQuery(id+"F3.opExtrude","SWEPT_FACE",FACE,{"disambiguationData":[OSD([sQuery(id+"F2.wireOp",EDGE,"E22.MirrorCS")])]})]});
            var Q2;
            Q2=makeQuery(id+"F3.boolean.opBoolean","INTERSECT",EDGE,{"derivedFrom":[makeQuery(id+"F1.opExtrude","SWEPT_FACE",FACE,{"disambiguationData":[OSD([sQuery(id+"F0.wireOp",EDGE,"E0.right")])]}),makeQuery(id+"F3.opExtrude","SWEPT_FACE",FACE,{"disambiguationData":[OSD([sQuery(id+"F2.wireOp",EDGE,"E8")])]})]});
            var Q3;
            Q3=makeQuery(id+"F6.boolean.opBoolean","INTERSECT",EDGE,{"derivedFrom":[makeQuery(id+"F4.opFillet","BLEND_FACE",FACE,{"disambiguationData":[OSD([sQuery(id+"F2.wireOp",EDGE,"E8"),sQuery(id+"F2.wireOp",EDGE,"E9")])]}),makeQuery(id+"F6.opExtrude","SWEPT_FACE",FACE,{"disambiguationData":[OSD([sQuery(id+"F5.wireOp",EDGE,"E30.right")])]})]});
            var Q4;
            Q4=makeQuery(id+"F6.boolean.opBoolean","INTERSECT",EDGE,{"derivedFrom":[makeQuery(id+"F3.boolean.opBoolean","COPY",FACE,{"derivedFrom":makeQuery(id+"F3.opExtrude","SWEPT_FACE",FACE,{"disambiguationData":[OSD([sQuery(id+"F2.wireOp",EDGE,"E9")])]})}),makeQuery(id+"F6.opExtrude","SWEPT_FACE",FACE,{"disambiguationData":[OSD([sQuery(id+"F5.wireOp",EDGE,"E30.left")])]})]});
            var Q5;
            Q5=makeQuery(id+"F3.boolean.opBoolean","COPY",EDGE,{"derivedFrom":makeQuery(id+"F3.opExtrude","CAP_EDGE",EDGE,{"disambiguationData":[OSD([sQuery(id+"F2.wireOp",EDGE,"E8")])],"isStart":true})});
            var Q6;
            Q6=makeQuery(id+"F6.boolean.opBoolean","INTERSECT",EDGE,{"derivedFrom":[makeQuery(id+"F3.boolean.opBoolean","COPY",FACE,{"derivedFrom":makeQuery(id+"F3.opExtrude","SWEPT_FACE",FACE,{"disambiguationData":[OSD([sQuery(id+"F2.wireOp",EDGE,"E22.MirrorCS")])]})}),makeQuery(id+"F6.opExtrude","SWEPT_FACE",FACE,{"disambiguationData":[OSD([sQuery(id+"F5.wireOp",EDGE,"E30.left")])]})]});
            var Q7;
            Q7=makeQuery(id+"F3.boolean.opBoolean","COPY",EDGE,{"derivedFrom":makeQuery(id+"F3.opExtrude","CAP_EDGE",EDGE,{"disambiguationData":[OSD([sQuery(id+"F2.wireOp",EDGE,"E21.MirrorCS")])],"isStart":true})});
            var Q8;
            {var subQ0=makeQuery(id+"F1.opExtrude","SWEPT_FACE",FACE,{"disambiguationData":[OSD([sQuery(id+"F0.wireOp",EDGE,"E0.left")])]});var subQ1=sQuery(id+"F2.wireOp",EDGE,"E20.MirrorCS");var subQ5=sQuery(id+"F2.wireOp",EDGE,"E26.MirrorCS");Q8=makeQuery(id+"F11.opFillet","BLEND_EDGE",EDGE,{"blendedFrom":[makeQuery(id+"F8.boolean.opBoolean","SPLIT",EDGE,{"disambiguationData":[TD([subQ0])],"derivedFrom":makeQuery(id+"F6.boolean.opBoolean","SPLIT",EDGE,{"disambiguationData":[TD([subQ0])],"derivedFrom":makeQuery(id+"F3.boolean.opBoolean","COPY",EDGE,{"derivedFrom":makeQuery(id+"F3.opExtrude","SWEPT_EDGE",EDGE,{"disambiguationData":[OSD([subQ1,subQ5])]})})})}),subQ0],"blendedInto":[subQ0]});}
            fillet(context, id + "F14", {"entities" : qUnion([Q0, Q1, Q2, Q3, Q4, Q5, Q6, Q7, Q8]), "radius" : 1 * mm, "tangentPropagation" : true, "allowEdgeOverflow" : false});
        }
        {
            var Q0;
            Q0=makeQuery(id+"F8.boolean.opBoolean","COPY",EDGE,{"derivedFrom":makeQuery(id+"F8.opExtrude","CAP_EDGE",EDGE,{"disambiguationData":[OSD([sQuery(id+"F7.wireOp",EDGE,"E40")])],"isStart":true})});
            var Q1;
            {var subQ3=sQuery(id+"F2.wireOp",EDGE,"E13");var subQ5=sQuery(id+"F2.wireOp",EDGE,"E12");var subQ6=makeQuery(id+"F3.boolean.opBoolean","COPY",FACE,{"derivedFrom":makeQuery(id+"F3.opExtrude","SWEPT_FACE",FACE,{"disambiguationData":[OSD([subQ5])]})});var subQ9=makeQuery(id+"F8.opExtrude","SWEPT_FACE",FACE,{"disambiguationData":[OSD([sQuery(id+"F7.wireOp",EDGE,"E42")])]});var subQ10=makeQuery(id+"F1.opExtrude","SWEPT_FACE",FACE,{"disambiguationData":[OSD([sQuery(id+"F0.wireOp",EDGE,"E0.left")])]});Q1=makeQuery(id+"F11.opFillet","BLEND_EDGE",EDGE,{"blendedFrom":[makeQuery(id+"F8.boolean.opBoolean","SPLIT",EDGE,{"disambiguationData":[TD([subQ10])],"derivedFrom":makeQuery(id+"F6.boolean.opBoolean","SPLIT",EDGE,{"disambiguationData":[TD([subQ10])],"derivedFrom":makeQuery(id+"F3.boolean.opBoolean","COPY",EDGE,{"derivedFrom":makeQuery(id+"F3.opExtrude","SWEPT_EDGE",EDGE,{"disambiguationData":[OSD([subQ5,subQ3])]})})})}),makeQuery(id+"F10.boolean.opBoolean","SPLIT",FACE,{"disambiguationData":[TD([subQ6])],"derivedFrom":makeQuery(id+"F8.boolean.opBoolean","COPY",FACE,{"disambiguationData":[TD([subQ6])],"derivedFrom":subQ9})})],"blendedInto":[makeQuery(id+"F10.boolean.opBoolean","SPLIT",FACE,{"disambiguationData":[TD([subQ6])],"derivedFrom":makeQuery(id+"F8.boolean.opBoolean","COPY",FACE,{"disambiguationData":[TD([subQ6])],"derivedFrom":subQ9})})]});}
            var Q2;
            {var subQ2=sQuery(id+"F2.wireOp",EDGE,"E25.MirrorCS");var subQ3=makeQuery(id+"F3.boolean.opBoolean","COPY",FACE,{"derivedFrom":makeQuery(id+"F3.opExtrude","SWEPT_FACE",FACE,{"disambiguationData":[OSD([subQ2])]})});var subQ4=sQuery(id+"F2.wireOp",EDGE,"E28.MirrorCS");var subQ9=makeQuery(id+"F8.opExtrude","SWEPT_FACE",FACE,{"disambiguationData":[OSD([sQuery(id+"F7.wireOp",EDGE,"E42")])]});var subQ10=makeQuery(id+"F1.opExtrude","SWEPT_FACE",FACE,{"disambiguationData":[OSD([sQuery(id+"F0.wireOp",EDGE,"E0.left")])]});Q2=makeQuery(id+"F11.opFillet","BLEND_EDGE",EDGE,{"blendedFrom":[makeQuery(id+"F8.boolean.opBoolean","SPLIT",EDGE,{"disambiguationData":[TD([subQ10])],"derivedFrom":makeQuery(id+"F6.boolean.opBoolean","SPLIT",EDGE,{"disambiguationData":[TD([subQ10])],"derivedFrom":makeQuery(id+"F3.boolean.opBoolean","COPY",EDGE,{"derivedFrom":makeQuery(id+"F3.opExtrude","SWEPT_EDGE",EDGE,{"disambiguationData":[OSD([subQ2,subQ4])]})})})}),makeQuery(id+"F10.boolean.opBoolean","SPLIT",FACE,{"disambiguationData":[TD([subQ3])],"derivedFrom":makeQuery(id+"F8.boolean.opBoolean","COPY",FACE,{"disambiguationData":[TD([makeQuery(id+"F3.boolean.opBoolean","COPY",FACE,{"derivedFrom":makeQuery(id+"F3.opExtrude","SWEPT_FACE",FACE,{"disambiguationData":[OSD([sQuery(id+"F2.wireOp",EDGE,"E20.MirrorCS")])]})})])],"derivedFrom":subQ9})})],"blendedInto":[makeQuery(id+"F10.boolean.opBoolean","SPLIT",FACE,{"disambiguationData":[TD([subQ3])],"derivedFrom":makeQuery(id+"F8.boolean.opBoolean","COPY",FACE,{"disambiguationData":[TD([makeQuery(id+"F3.boolean.opBoolean","COPY",FACE,{"derivedFrom":makeQuery(id+"F3.opExtrude","SWEPT_FACE",FACE,{"disambiguationData":[OSD([sQuery(id+"F2.wireOp",EDGE,"E20.MirrorCS")])]})})])],"derivedFrom":subQ9})})]});}
            var Q3;
            {var subQ2=sQuery(id+"F2.wireOp",EDGE,"E25.MirrorCS");var subQ3=makeQuery(id+"F3.boolean.opBoolean","COPY",FACE,{"derivedFrom":makeQuery(id+"F3.opExtrude","SWEPT_FACE",FACE,{"disambiguationData":[OSD([subQ2])]})});var subQ4=sQuery(id+"F2.wireOp",EDGE,"E28.MirrorCS");var subQ9=makeQuery(id+"F3.boolean.opBoolean","COPY",FACE,{"derivedFrom":makeQuery(id+"F3.opExtrude","SWEPT_FACE",FACE,{"disambiguationData":[OSD([sQuery(id+"F2.wireOp",EDGE,"E20.MirrorCS")])]})});var subQ13=makeQuery(id+"F8.opExtrude","SWEPT_FACE",FACE,{"disambiguationData":[OSD([sQuery(id+"F7.wireOp",EDGE,"E40")])]});var subQ14=sQuery(id+"F0.wireOp",EDGE,"E0.right");var subQ15=makeQuery(id+"F6.opExtrude","SWEPT_FACE",FACE,{"disambiguationData":[OSD([sQuery(id+"F5.wireOp",EDGE,"E30.right")])]});Q3=makeQuery(id+"F11.opFillet","BLEND_EDGE",EDGE,{"blendedFrom":[makeQuery(id+"F8.boolean.opBoolean","SPLIT",EDGE,{"disambiguationData":[TD([makeQuery(id+"F6.boolean.opBoolean","COPY",FACE,{"disambiguationData":[TD([subQ9])],"derivedFrom":subQ15})])],"derivedFrom":makeQuery(id+"F6.boolean.opBoolean","SPLIT",EDGE,{"disambiguationData":[TD([makeQuery(id+"F1.opExtrude","SWEPT_FACE",FACE,{"disambiguationData":[OSD([subQ14])]})])],"derivedFrom":makeQuery(id+"F3.boolean.opBoolean","COPY",EDGE,{"derivedFrom":makeQuery(id+"F3.opExtrude","SWEPT_EDGE",EDGE,{"disambiguationData":[OSD([subQ2,subQ4])]})})})}),makeQuery(id+"F10.boolean.opBoolean","SPLIT",FACE,{"disambiguationData":[TD([subQ3])],"derivedFrom":makeQuery(id+"F8.boolean.opBoolean","COPY",FACE,{"disambiguationData":[TD([subQ9])],"derivedFrom":subQ13})})],"blendedInto":[makeQuery(id+"F10.boolean.opBoolean","SPLIT",FACE,{"disambiguationData":[TD([subQ3])],"derivedFrom":makeQuery(id+"F8.boolean.opBoolean","COPY",FACE,{"disambiguationData":[TD([subQ9])],"derivedFrom":subQ13})})]});}
            var Q4;
            {var subQ2=sQuery(id+"F2.wireOp",EDGE,"E18");var subQ4=sQuery(id+"F2.wireOp",EDGE,"E17");var subQ5=makeQuery(id+"F3.boolean.opBoolean","COPY",FACE,{"derivedFrom":makeQuery(id+"F3.opExtrude","SWEPT_FACE",FACE,{"disambiguationData":[OSD([subQ4])]})});var subQ9=makeQuery(id+"F3.boolean.opBoolean","COPY",FACE,{"derivedFrom":makeQuery(id+"F3.opExtrude","SWEPT_FACE",FACE,{"disambiguationData":[OSD([sQuery(id+"F2.wireOp",EDGE,"E12")])]})});var subQ11=sQuery(id+"F2.wireOp",EDGE,"E8");var subQ13=makeQuery(id+"F8.opExtrude","SWEPT_FACE",FACE,{"disambiguationData":[OSD([sQuery(id+"F7.wireOp",EDGE,"E40")])]});var subQ14=sQuery(id+"F0.wireOp",EDGE,"E0.right");var subQ15=makeQuery(id+"F6.opExtrude","SWEPT_FACE",FACE,{"disambiguationData":[OSD([sQuery(id+"F5.wireOp",EDGE,"E30.right")])]});Q4=makeQuery(id+"F11.opFillet","BLEND_EDGE",EDGE,{"blendedFrom":[makeQuery(id+"F8.boolean.opBoolean","SPLIT",EDGE,{"disambiguationData":[TD([makeQuery(id+"F6.boolean.opBoolean","COPY",FACE,{"disambiguationData":[TD([makeQuery(id+"F3.boolean.opBoolean","COPY",FACE,{"derivedFrom":makeQuery(id+"F3.opExtrude","SWEPT_FACE",FACE,{"disambiguationData":[OSD([subQ11])]})})])],"derivedFrom":subQ15})])],"derivedFrom":makeQuery(id+"F6.boolean.opBoolean","SPLIT",EDGE,{"disambiguationData":[TD([makeQuery(id+"F1.opExtrude","SWEPT_FACE",FACE,{"disambiguationData":[OSD([subQ14])]})])],"derivedFrom":makeQuery(id+"F3.boolean.opBoolean","COPY",EDGE,{"derivedFrom":makeQuery(id+"F3.opExtrude","SWEPT_EDGE",EDGE,{"disambiguationData":[OSD([subQ4,subQ2])]})})})}),makeQuery(id+"F10.boolean.opBoolean","SPLIT",FACE,{"disambiguationData":[TD([subQ5])],"derivedFrom":makeQuery(id+"F8.boolean.opBoolean","COPY",FACE,{"disambiguationData":[TD([subQ9])],"derivedFrom":subQ13})})],"blendedInto":[makeQuery(id+"F10.boolean.opBoolean","SPLIT",FACE,{"disambiguationData":[TD([subQ5])],"derivedFrom":makeQuery(id+"F8.boolean.opBoolean","COPY",FACE,{"disambiguationData":[TD([subQ9])],"derivedFrom":subQ13})})]});}
            var Q5;
            {var subQ0=sQuery(id+"F2.wireOp",EDGE,"E26.MirrorCS");var subQ3=sQuery(id+"F2.wireOp",EDGE,"E20.MirrorCS");var subQ4=makeQuery(id+"F3.boolean.opBoolean","COPY",FACE,{"derivedFrom":makeQuery(id+"F3.opExtrude","SWEPT_FACE",FACE,{"disambiguationData":[OSD([subQ3])]})});var subQ13=makeQuery(id+"F8.opExtrude","SWEPT_FACE",FACE,{"disambiguationData":[OSD([sQuery(id+"F7.wireOp",EDGE,"E40")])]});var subQ14=sQuery(id+"F0.wireOp",EDGE,"E0.right");var subQ15=makeQuery(id+"F6.opExtrude","SWEPT_FACE",FACE,{"disambiguationData":[OSD([sQuery(id+"F5.wireOp",EDGE,"E30.right")])]});Q5=makeQuery(id+"F11.opFillet","BLEND_EDGE",EDGE,{"blendedFrom":[makeQuery(id+"F8.boolean.opBoolean","SPLIT",EDGE,{"disambiguationData":[TD([makeQuery(id+"F6.boolean.opBoolean","COPY",FACE,{"disambiguationData":[TD([subQ4])],"derivedFrom":subQ15})])],"derivedFrom":makeQuery(id+"F6.boolean.opBoolean","SPLIT",EDGE,{"disambiguationData":[TD([makeQuery(id+"F1.opExtrude","SWEPT_FACE",FACE,{"disambiguationData":[OSD([subQ14])]})])],"derivedFrom":makeQuery(id+"F3.boolean.opBoolean","COPY",EDGE,{"derivedFrom":makeQuery(id+"F3.opExtrude","SWEPT_EDGE",EDGE,{"disambiguationData":[OSD([subQ3,subQ0])]})})})}),makeQuery(id+"F10.boolean.opBoolean","SPLIT",FACE,{"disambiguationData":[TD([subQ4])],"derivedFrom":makeQuery(id+"F8.boolean.opBoolean","COPY",FACE,{"disambiguationData":[TD([subQ4])],"derivedFrom":subQ13})})],"blendedInto":[makeQuery(id+"F10.boolean.opBoolean","SPLIT",FACE,{"disambiguationData":[TD([subQ4])],"derivedFrom":makeQuery(id+"F8.boolean.opBoolean","COPY",FACE,{"disambiguationData":[TD([subQ4])],"derivedFrom":subQ13})})]});}
            var Q6;
            {var subQ0=sQuery(id+"F2.wireOp",EDGE,"E26.MirrorCS");var subQ3=sQuery(id+"F2.wireOp",EDGE,"E20.MirrorCS");var subQ4=makeQuery(id+"F3.boolean.opBoolean","COPY",FACE,{"derivedFrom":makeQuery(id+"F3.opExtrude","SWEPT_FACE",FACE,{"disambiguationData":[OSD([subQ3])]})});var subQ9=makeQuery(id+"F8.opExtrude","SWEPT_FACE",FACE,{"disambiguationData":[OSD([sQuery(id+"F7.wireOp",EDGE,"E42")])]});var subQ10=makeQuery(id+"F1.opExtrude","SWEPT_FACE",FACE,{"disambiguationData":[OSD([sQuery(id+"F0.wireOp",EDGE,"E0.left")])]});Q6=makeQuery(id+"F11.opFillet","BLEND_EDGE",EDGE,{"blendedFrom":[makeQuery(id+"F8.boolean.opBoolean","SPLIT",EDGE,{"disambiguationData":[TD([subQ10])],"derivedFrom":makeQuery(id+"F6.boolean.opBoolean","SPLIT",EDGE,{"disambiguationData":[TD([subQ10])],"derivedFrom":makeQuery(id+"F3.boolean.opBoolean","COPY",EDGE,{"derivedFrom":makeQuery(id+"F3.opExtrude","SWEPT_EDGE",EDGE,{"disambiguationData":[OSD([subQ3,subQ0])]})})})}),makeQuery(id+"F10.boolean.opBoolean","SPLIT",FACE,{"disambiguationData":[TD([subQ4])],"derivedFrom":makeQuery(id+"F8.boolean.opBoolean","COPY",FACE,{"disambiguationData":[TD([subQ4])],"derivedFrom":subQ9})})],"blendedInto":[makeQuery(id+"F10.boolean.opBoolean","SPLIT",FACE,{"disambiguationData":[TD([subQ4])],"derivedFrom":makeQuery(id+"F8.boolean.opBoolean","COPY",FACE,{"disambiguationData":[TD([subQ4])],"derivedFrom":subQ9})})]});}
            var Q7;
            {var subQ2=sQuery(id+"F2.wireOp",EDGE,"E18");var subQ4=sQuery(id+"F2.wireOp",EDGE,"E17");var subQ5=makeQuery(id+"F3.boolean.opBoolean","COPY",FACE,{"derivedFrom":makeQuery(id+"F3.opExtrude","SWEPT_FACE",FACE,{"disambiguationData":[OSD([subQ4])]})});var subQ9=makeQuery(id+"F8.opExtrude","SWEPT_FACE",FACE,{"disambiguationData":[OSD([sQuery(id+"F7.wireOp",EDGE,"E42")])]});var subQ10=makeQuery(id+"F1.opExtrude","SWEPT_FACE",FACE,{"disambiguationData":[OSD([sQuery(id+"F0.wireOp",EDGE,"E0.left")])]});Q7=makeQuery(id+"F11.opFillet","BLEND_EDGE",EDGE,{"blendedFrom":[makeQuery(id+"F8.boolean.opBoolean","SPLIT",EDGE,{"disambiguationData":[TD([subQ10])],"derivedFrom":makeQuery(id+"F6.boolean.opBoolean","SPLIT",EDGE,{"disambiguationData":[TD([subQ10])],"derivedFrom":makeQuery(id+"F3.boolean.opBoolean","COPY",EDGE,{"derivedFrom":makeQuery(id+"F3.opExtrude","SWEPT_EDGE",EDGE,{"disambiguationData":[OSD([subQ4,subQ2])]})})})}),makeQuery(id+"F10.boolean.opBoolean","SPLIT",FACE,{"disambiguationData":[TD([subQ5])],"derivedFrom":makeQuery(id+"F8.boolean.opBoolean","COPY",FACE,{"disambiguationData":[TD([makeQuery(id+"F3.boolean.opBoolean","COPY",FACE,{"derivedFrom":makeQuery(id+"F3.opExtrude","SWEPT_FACE",FACE,{"disambiguationData":[OSD([sQuery(id+"F2.wireOp",EDGE,"E12")])]})})])],"derivedFrom":subQ9})})],"blendedInto":[makeQuery(id+"F10.boolean.opBoolean","SPLIT",FACE,{"disambiguationData":[TD([subQ5])],"derivedFrom":makeQuery(id+"F8.boolean.opBoolean","COPY",FACE,{"disambiguationData":[TD([makeQuery(id+"F3.boolean.opBoolean","COPY",FACE,{"derivedFrom":makeQuery(id+"F3.opExtrude","SWEPT_FACE",FACE,{"disambiguationData":[OSD([sQuery(id+"F2.wireOp",EDGE,"E12")])]})})])],"derivedFrom":subQ9})})]});}
            fillet(context, id + "F15", {"entities" : qUnion([Q0, Q1, Q2, Q3, Q4, Q5, Q6, Q7]), "radius" : 2 * mm, "tangentPropagation" : true, "allowEdgeOverflow" : false});
        }
    });
